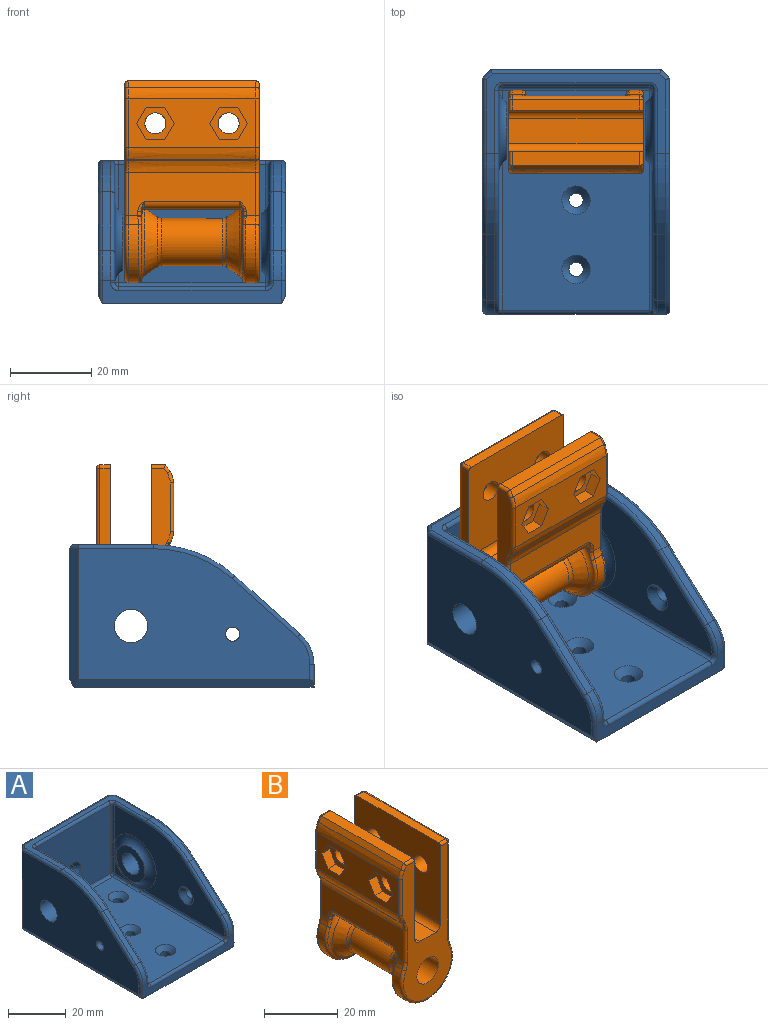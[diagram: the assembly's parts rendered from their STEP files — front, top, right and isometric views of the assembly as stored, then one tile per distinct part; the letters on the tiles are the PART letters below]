
ASSEMBLY  parts=2 mates=1
PART A: 87 faces, bbox 46x60.8x37.5 mm
  f0: plane 54x29mm, normal (1,0,0), area 820.2mm2, adj f28,f38,f46,f47,f48,f52,f57,f61
  f1: plane 54x29mm, normal (-1,0,0), area 820.2mm2, adj f31,f37,f59,f66,f67,f69,f71,f72
  f2: cylinder r=1.75mm len=3.5mm, axis (0,0,1), area 24.7mm2, adj f3,f6
  f3: cone r=1.75mm half-angle=45deg, axis (0,0,1), area 40.8mm2, adj f2,f11
  f4: plane 44x19.56mm, normal (0,0,1), area 157.9mm2, adj f39,f40,f62,f65,f68,f70,f72,f78
  f5: plane 57x32.27mm, normal (-1,0,0), area 1425.6mm2, adj f15,f27,f34,f36,f82,f83,f84,f85
  f6: plane 59x44mm, normal (0,0,-1), area 2557.5mm2, adj f2,f8,f17,f19,f21,f32,f33,f34
  f7: plane 57x32.27mm, normal (1,0,0), area 1425.6mm2, adj f14,f30,f32,f35,f74,f75,f76,f77
  f8: plane 44x5.52mm, normal (0,-1,0), area 143.8mm2, adj f6,f41,f42,f47,f53,f58,f63,f66
  f9: plane 42x32.27mm, normal (0,1,0), area 1345.6mm2, adj f23,f33,f35,f36,f80
  f10: plane 6.92x6.92mm, normal (1,0,0), area 15.9mm2, adj f38,f43,f51
  f11: plane 54x36mm, normal (0,0,1), area 1789.8mm2, adj f3,f18,f20,f22,f43,f44,f48,f49
  f12: plane 6.92x6.92mm, normal (-1,0,0), area 15.9mm2, adj f37,f49,f60
  f13: plane 36x29mm, normal (0,-1,0), area 1005.3mm2, adj f24,f50,f51,f56,f60,f61,f64,f67
  f14: cylinder r=4.1mm len=8.2mm, axis (-1,0,0), area 154.6mm2, adj f7,f29
  f15: cylinder r=4.1mm len=8.2mm, axis (-1,0,0), area 154.6mm2, adj f5,f16
  f16: plane 14x14mm, normal (1,0,0), area 101.1mm2, adj f15,f38
  f17: cylinder r=1.75mm len=3.5mm, axis (0,0,1), area 24.7mm2, adj f6,f18
  f18: cone r=1.75mm half-angle=45deg, axis (0,0,1), area 40.8mm2, adj f11,f17
  f19: cylinder r=1.75mm len=3.5mm, axis (0,0,1), area 24.7mm2, adj f6,f20
  f20: cone r=1.75mm half-angle=45deg, axis (0,0,1), area 40.8mm2, adj f11,f19
  f21: cylinder r=1.75mm len=3.5mm, axis (0,0,1), area 24.7mm2, adj f6,f22
  f22: cone r=1.75mm half-angle=45deg, axis (0,0,1), area 40.8mm2, adj f11,f21
  f23: cylinder r=1.75mm len=3.5mm, axis (0,-1,0), area 24.7mm2, adj f9,f24
  f24: cone r=1.75mm half-angle=45deg, axis (0,-1,0), area 40.8mm2, adj f13,f23
  f25: plane 16.12x14.4mm, normal (0,-0.67,0.75), area 43.2mm2, adj f39,f41,f52,f84
  f26: plane 16.12x14.4mm, normal (0,-0.67,0.75), area 43.2mm2, adj f40,f42,f71,f76
  f27: cylinder r=1.75mm len=3.5mm, axis (1,0,0), area 24.7mm2, adj f5,f28
  f28: cone r=1.75mm half-angle=45deg, axis (1,0,0), area 40.8mm2, adj f0,f27
  f29: plane 14x14mm, normal (-1,0,0), area 101.1mm2, adj f14,f37
  f30: cylinder r=1.75mm len=3.5mm, axis (-1,0,0), area 24.7mm2, adj f7,f31
  f31: cone r=1.75mm half-angle=45deg, axis (-1,0,0), area 40.8mm2, adj f1,f30
  f32: plane 59x1.73mm, normal (0.87,0,-0.5), area 116.6mm2, adj f6,f7,f35,f74
  f33: plane 44x1.73mm, normal (0,0.87,-0.5), area 86mm2, adj f6,f9,f35,f36
  f34: plane 59x1.73mm, normal (-0.87,0,-0.5), area 116.6mm2, adj f5,f6,f36,f86
  f35: plane 34x2mm, normal (0.71,0.71,0), area 93.7mm2, adj f7,f9,f32,f33,f79
  f36: plane 34x2mm, normal (-0.71,0.71,0), area 93.7mm2, adj f5,f9,f33,f34,f81
  f37: torus R=10.46mm, axis (1,0,0), area 220mm2, adj f1,f12,f29,f54,f64
  f38: torus R=10.46mm, axis (1,0,0), area 220mm2, adj f0,f10,f16,f44,f56
  f39: cylinder r=30mm len=19.98mm, axis (-1,0,0), area 43.7mm2, adj f4,f25,f57,f83
  f40: cylinder r=30mm len=19.98mm, axis (-1,0,0), area 43.7mm2, adj f4,f26,f73,f77
  f41: cylinder r=10mm len=7.46mm, axis (1,0,0), area 16.8mm2, adj f8,f25,f46,f85
  f42: cylinder r=10mm len=7.46mm, axis (1,0,0), area 16.8mm2, adj f8,f26,f69,f75
  f43: cylinder r=1mm len=6.92mm, axis (0,-1,0), area 10.9mm2, adj f10,f11,f44,f45
  f44: bspline ~7.51x1.17mm, area 10.3mm2, adj f11,f38,f43,f48
  f45: sphere r=1mm, area 1.6mm2, adj f43,f50,f51
  f46: torus R=9mm, axis (1,0,0), area 12.7mm2, adj f0,f41,f47,f52
  f47: cylinder r=1mm len=1mm, axis (0,0,-1), area 0.8mm2, adj f0,f8,f46,f53
  f48: cylinder r=1mm len=40.92mm, axis (0,-1,0), area 64.3mm2, adj f0,f11,f44,f53
  f49: cylinder r=1mm len=6.92mm, axis (0,1,0), area 10.9mm2, adj f11,f12,f54,f55
  f50: cylinder r=1mm len=36mm, axis (-1,0,0), area 56.5mm2, adj f11,f13,f45,f55
  f51: cylinder r=1mm len=6.92mm, axis (0,0,1), area 10.9mm2, adj f10,f13,f45,f56
  f52: cylinder r=1mm len=16.79mm, axis (0,0.75,0.67), area 34mm2, adj f0,f25,f46,f57
  f53: torus R=2mm, axis (0,-1,0), area 3.4mm2, adj f8,f47,f48,f58
  f54: bspline ~8.32x1.17mm, area 10.3mm2, adj f11,f37,f49,f59
  f55: sphere r=1mm, area 1.6mm2, adj f49,f50,f60
  f56: bspline ~8.32x1.17mm, area 10.3mm2, adj f13,f38,f51,f61
  f57: torus R=29mm, axis (1,0,0), area 33.9mm2, adj f0,f39,f52,f62
  f58: cylinder r=1mm len=36mm, axis (1,0,0), area 56.5mm2, adj f8,f11,f53,f63
  f59: cylinder r=1mm len=40.92mm, axis (0,1,0), area 64.3mm2, adj f1,f11,f54,f63
  f60: cylinder r=1mm len=6.92mm, axis (0,0,-1), area 10.9mm2, adj f12,f13,f55,f64
  f61: cylinder r=1mm len=15.92mm, axis (0,0,1), area 25mm2, adj f0,f13,f56,f65
  f62: cylinder r=1mm len=15.56mm, axis (0,1,0), area 24.4mm2, adj f0,f4,f57,f65
  f63: torus R=2mm, axis (0,-1,0), area 3.4mm2, adj f8,f58,f59,f66
  f64: bspline ~8.32x1.17mm, area 10.3mm2, adj f13,f37,f60,f67
  f65: torus R=2mm, axis (0,0,1), area 3.4mm2, adj f4,f61,f62,f68
  f66: cylinder r=1mm len=1mm, axis (0,0,1), area 0.8mm2, adj f1,f8,f63,f69
  f67: cylinder r=1mm len=15.92mm, axis (0,0,-1), area 25mm2, adj f1,f13,f64,f70
  f68: cylinder r=1mm len=36mm, axis (1,0,0), area 56.5mm2, adj f4,f13,f65,f70
  f69: torus R=9mm, axis (1,0,0), area 12.7mm2, adj f1,f42,f66,f71
  f70: torus R=2mm, axis (0,0,1), area 3.4mm2, adj f4,f67,f68,f72
  f71: cylinder r=1mm len=16.79mm, axis (0,0.75,0.67), area 34mm2, adj f1,f26,f69,f73
  f72: cylinder r=1mm len=15.56mm, axis (0,-1,0), area 24.4mm2, adj f1,f4,f70,f73
  f73: torus R=29mm, axis (1,0,0), area 33.9mm2, adj f1,f40,f71,f72
  f74: cylinder r=1mm len=5.52mm, axis (0,0,-1), area 6.9mm2, adj f7,f8,f32,f75
  f75: torus R=9mm, axis (1,0,0), area 12.7mm2, adj f7,f42,f74,f76
  f76: cylinder r=1mm len=16.79mm, axis (0,0.75,0.67), area 34mm2, adj f7,f26,f75,f77
  f77: torus R=29mm, axis (1,0,0), area 33.9mm2, adj f7,f40,f76,f78
  f78: cylinder r=1mm len=18.56mm, axis (0,1,0), area 28.9mm2, adj f4,f7,f77,f79
  f79: cylinder r=1mm len=2.71mm, axis (-0.71,0.71,0), area 4mm2, adj f4,f35,f78,f80
  f80: cylinder r=1mm len=42mm, axis (-1,0,0), area 65.5mm2, adj f4,f9,f79,f81
  f81: cylinder r=1mm len=2.71mm, axis (0.71,0.71,0), area 4mm2, adj f4,f36,f80,f82
  f82: cylinder r=1mm len=18.56mm, axis (0,-1,0), area 28.9mm2, adj f4,f5,f81,f83
  f83: torus R=29mm, axis (1,0,0), area 33.9mm2, adj f5,f39,f82,f84
  f84: cylinder r=1mm len=16.79mm, axis (0,0.75,0.67), area 34mm2, adj f5,f25,f83,f85
  f85: torus R=9mm, axis (1,0,0), area 12.7mm2, adj f5,f41,f84,f86
  f86: cylinder r=1mm len=5.52mm, axis (0,0,1), area 6.9mm2, adj f5,f8,f34,f85
PART B: 113 faces, bbox 24.6x36.3x51.9 mm
  f0: plane 1.29x0.97mm, normal (0,1,0), area 0.6mm2, adj f44,f109,f110,f111
  f1: plane 1.29x0.97mm, normal (0,-1,0), area 0.6mm2, adj f45,f95,f96,f98
  f2: cylinder r=10mm len=20mm, axis (0,1,0), area 101.1mm2, adj f50,f52,f75,f92
  f3: plane 31.4x11.99mm, normal (-1,0,0), area 265.7mm2, adj f20,f21,f22,f23,f24,f25,f28,f29
  f4: cylinder r=2.6mm len=5.2mm, axis (-1,0,0), area 40.8mm2, adj f6,f34
  f5: cylinder r=2.6mm len=5.2mm, axis (-1,0,0), area 40.8mm2, adj f6,f26
  f6: plane 33x26.5mm, normal (1,0,0), area 831.8mm2, adj f4,f5,f7,f17,f18,f48,f56,f82
  f7: plane 31.4x3.5mm, normal (0,0,1), area 109.9mm2, adj f6,f8,f56,f82
  f8: plane 31.4x1.57mm, normal (-0.82,0,0.57), area 60mm2, adj f7,f54,f57,f84
  f9: plane 31.4x0.27mm, normal (-0.82,0,-0.57), area 10.5mm2, adj f53,f55,f61,f79
  f10: plane 31.4x10.63mm, normal (-1,0,0), area 242.1mm2, adj f41,f49,f50,f55,f63,f77,f97,f98
  f11: cylinder r=10mm len=20mm, axis (0,1,0), area 101.1mm2, adj f49,f51,f65,f105
  f12: plane 32.26x31.4mm, normal (1,0,0), area 878.9mm2, adj f19,f27,f42,f51,f52,f67,f70,f73
  f13: plane 31.4x2.7mm, normal (0,0,1), area 84.8mm2, adj f14,f68,f70,f71
  f14: plane 33x26.5mm, normal (-1,0,0), area 831.8mm2, adj f13,f17,f18,f19,f27,f47,f68,f71
  f15: plane 33x6mm, normal (0,0,1), area 198mm2, adj f17,f18,f47,f48
  f16: cylinder r=4.1mm len=33mm, axis (0,1,0), area 850.1mm2, adj f17,f18
  f17: plane 48x18.9mm, normal (0,-1,0), area 447.9mm2, adj f6,f14,f15,f16,f47,f48,f56,f57
  f18: plane 48x18.9mm, normal (0,1,0), area 447.9mm2, adj f6,f14,f15,f16,f47,f48,f71,f73
  f19: cylinder r=2.6mm len=5.2mm, axis (-1,0,0), area 57.2mm2, adj f12,f14
  f20: plane 4.62x3mm, normal (0,0,-1), area 13.9mm2, adj f3,f21,f25,f26
  f21: plane 4x3mm, normal (0,-0.87,-0.5), area 13.9mm2, adj f3,f20,f22,f26
  f22: plane 4x3mm, normal (0,-0.87,0.5), area 13.9mm2, adj f3,f21,f23,f26
  f23: plane 4.62x3mm, normal (0,0,1), area 13.9mm2, adj f3,f22,f24,f26
  f24: plane 4x3mm, normal (0,0.87,0.5), area 13.9mm2, adj f3,f23,f25,f26
  f25: plane 4x3mm, normal (0,0.87,-0.5), area 13.9mm2, adj f3,f20,f24,f26
  f26: plane 9.24x8mm, normal (-1,0,0), area 34.2mm2, adj f5,f20,f21,f22,f23,f24,f25
  f27: cylinder r=2.6mm len=5.2mm, axis (-1,0,0), area 57.2mm2, adj f12,f14
  f28: plane 4.62x3mm, normal (0,0,-1), area 13.9mm2, adj f3,f29,f33,f34
  f29: plane 4x3mm, normal (0,-0.87,-0.5), area 13.9mm2, adj f3,f28,f30,f34
  f30: plane 4x3mm, normal (0,-0.87,0.5), area 13.9mm2, adj f3,f29,f31,f34
  f31: plane 4.62x3mm, normal (0,0,1), area 13.9mm2, adj f3,f30,f32,f34
  f32: plane 4x3mm, normal (0,0.87,0.5), area 13.9mm2, adj f3,f31,f33,f34
  f33: plane 4x3mm, normal (0,0.87,-0.5), area 13.9mm2, adj f3,f28,f32,f34
  f34: plane 9.24x8mm, normal (-1,0,0), area 34.2mm2, adj f4,f28,f29,f30,f31,f32,f33
  f35: cylinder r=10mm len=22.89mm, axis (0,-1,0), area 262mm2, adj f41,f42,f91,f106
  f36: cylinder r=5.8mm len=14.88mm, axis (0,-1,0), area 542.4mm2, adj f43,f46
  f37: cone r=5.8mm half-angle=35deg, axis (0,-1,0), area 169.6mm2, adj f43,f44
  f38: plane 1.29x0.97mm, normal (0,1,0), area 0.6mm2, adj f44,f99,f101,f102
  f39: plane 1.29x0.97mm, normal (0,-1,0), area 0.6mm2, adj f45,f86,f87,f88
  f40: cone r=5.8mm half-angle=35deg, axis (0,1,0), area 169.6mm2, adj f45,f46
  f41: cylinder r=2mm len=23.4mm, axis (0,-1,0), area 100mm2, adj f10,f35,f93,f95,f108,f110
  f42: cylinder r=2mm len=23.4mm, axis (0,-1,0), area 100mm2, adj f12,f35,f87,f89,f102,f104
  f43: torus R=7.8mm, axis (0,-1,0), area 45.5mm2, adj f36,f37
  f44: torus R=9.94mm, axis (0,-1,0), area 70.7mm2, adj f0,f37,f38,f103,f104,f105,f106,f107
  f45: torus R=9.94mm, axis (0,1,0), area 70.7mm2, adj f1,f39,f40,f89,f90,f91,f92,f93
  f46: torus R=7.8mm, axis (0,-1,0), area 45.5mm2, adj f36,f40
  f47: cylinder r=2mm len=33mm, axis (0,1,0), area 103.7mm2, adj f14,f15,f17,f18
  f48: cylinder r=2mm len=33mm, axis (0,-1,0), area 103.7mm2, adj f6,f15,f17,f18
  f49: bspline ~4.4x2.18mm, area 5.5mm2, adj f10,f11,f64,f107,f109
  f50: bspline ~4.4x2.18mm, area 5.5mm2, adj f2,f10,f76,f94,f96
  f51: bspline ~4.4x2.18mm, area 5.5mm2, adj f11,f12,f66,f101,f103
  f52: bspline ~4.4x2.18mm, area 5.5mm2, adj f2,f12,f74,f88,f90
  f53: bspline ~36.3x2.87mm, area 95.1mm2, adj f3,f9,f60,f80
  f54: bspline ~36.3x2.87mm, area 95.1mm2, adj f3,f8,f58,f83
  f55: bspline ~36.3x2.87mm, area 95.1mm2, adj f9,f10,f62,f78
  f56: cylinder r=0.8mm len=3.5mm, axis (1,0,0), area 4.1mm2, adj f6,f7,f17,f57
  f57: cylinder r=0.8mm len=2.02mm, axis (0.57,0,0.82), area 2.1mm2, adj f8,f17,f56,f58
  f58: bspline ~3.38x1.72mm, area 3.6mm2, adj f17,f54,f57,f59
  f59: cylinder r=0.8mm len=11.99mm, axis (0,0,1), area 15.1mm2, adj f3,f17,f58,f60
  f60: bspline ~3.38x1.72mm, area 3.6mm2, adj f17,f53,f59,f61
  f61: cylinder r=0.8mm len=0.85mm, axis (-0.57,0,0.82), area 0.4mm2, adj f9,f17,f60,f62
  f62: bspline ~3.69x1.74mm, area 4mm2, adj f17,f55,f61,f63
  f63: cylinder r=0.8mm len=10.63mm, axis (0,0,1), area 13.4mm2, adj f10,f17,f62,f64
  f64: bspline ~3.09x1.43mm, area 3mm2, adj f17,f49,f63,f65
  f65: torus R=9.2mm, axis (0,-1,0), area 49.3mm2, adj f11,f17,f64,f66
  f66: bspline ~3.09x1.43mm, area 3mm2, adj f17,f51,f65,f67
  f67: cylinder r=0.8mm len=32.26mm, axis (0,0,-1), area 40.5mm2, adj f12,f17,f66,f69
  f68: cylinder r=0.8mm len=2.7mm, axis (1,0,0), area 3.4mm2, adj f13,f14,f17,f69
  f69: sphere r=0.8mm, area 1mm2, adj f67,f68,f70
  f70: cylinder r=0.8mm len=31.4mm, axis (0,1,0), area 39.5mm2, adj f12,f13,f69,f72
  f71: cylinder r=0.8mm len=2.7mm, axis (-1,0,0), area 3.4mm2, adj f13,f14,f18,f72
  f72: sphere r=0.8mm, area 0.6mm2, adj f70,f71,f73
  f73: cylinder r=0.8mm len=32.26mm, axis (0,0,1), area 40.5mm2, adj f12,f18,f72,f74
  f74: bspline ~3.09x1.43mm, area 3mm2, adj f18,f52,f73,f75
  f75: torus R=9.2mm, axis (0,-1,0), area 49.3mm2, adj f2,f18,f74,f76
  f76: bspline ~3.09x1.43mm, area 3mm2, adj f18,f50,f75,f77
  f77: cylinder r=0.8mm len=10.63mm, axis (0,0,-1), area 13.4mm2, adj f10,f18,f76,f78
  f78: bspline ~3.69x1.74mm, area 4mm2, adj f18,f55,f77,f79
  f79: cylinder r=0.8mm len=0.85mm, axis (0.57,0,-0.82), area 0.4mm2, adj f9,f18,f78,f80
  f80: bspline ~3.38x1.72mm, area 3.6mm2, adj f18,f53,f79,f81
  f81: cylinder r=0.8mm len=11.99mm, axis (0,0,-1), area 15.1mm2, adj f3,f18,f80,f83
  f82: cylinder r=0.8mm len=3.5mm, axis (-1,0,0), area 4.1mm2, adj f6,f7,f18,f84
  f83: bspline ~3.38x1.72mm, area 3.6mm2, adj f18,f54,f81,f84
  f84: cylinder r=0.8mm len=2.02mm, axis (-0.57,0,-0.82), area 2.1mm2, adj f8,f18,f82,f83
  f85: bspline ~3x1.6mm, area 1.3mm2, adj f12,f86,f87
  f86: cylinder r=0.8mm len=1.02mm, axis (0,0,1), area 1.3mm2, adj f12,f39,f85,f88
  f87: torus R=2.8mm, axis (0,1,0), area 2.5mm2, adj f39,f42,f85,f89
  f88: bspline ~0.9x0.85mm, area 0.3mm2, adj f39,f52,f86,f90
  f89: bspline ~2.2x1.65mm, area 2.5mm2, adj f42,f45,f87,f91
  f90: bspline ~2.65x1.45mm, area 2.4mm2, adj f45,f52,f88,f92
  f91: torus R=9.2mm, axis (0,-1,0), area 19.4mm2, adj f35,f45,f89,f93
  f92: torus R=9.2mm, axis (0,1,0), area 41.3mm2, adj f2,f45,f90,f94
  f93: bspline ~2.2x1.65mm, area 2.5mm2, adj f41,f45,f91,f95
  f94: bspline ~2.65x1.45mm, area 2.4mm2, adj f45,f50,f92,f96
  f95: torus R=2.8mm, axis (0,1,0), area 2.5mm2, adj f1,f41,f93,f97
  f96: bspline ~0.83x0.8mm, area 0.3mm2, adj f1,f50,f94,f98
  f97: bspline ~3x1.6mm, area 1.3mm2, adj f10,f95,f98
  f98: cylinder r=0.8mm len=1.02mm, axis (0,0,1), area 1.3mm2, adj f1,f10,f96,f97
  f99: cylinder r=0.8mm len=1.02mm, axis (0,0,-1), area 1.3mm2, adj f12,f38,f100,f101
  f100: bspline ~3x1.6mm, area 1.3mm2, adj f12,f99,f102
  f101: bspline ~0.83x0.8mm, area 0.3mm2, adj f38,f51,f99,f103
  f102: torus R=2.8mm, axis (0,-1,0), area 2.5mm2, adj f38,f42,f100,f104
  f103: bspline ~2.44x1.35mm, area 2.4mm2, adj f44,f51,f101,f105
  f104: bspline ~2.2x1.65mm, area 2.5mm2, adj f42,f44,f102,f106
  f105: torus R=9.2mm, axis (0,1,0), area 41.3mm2, adj f11,f44,f103,f107
  f106: torus R=9.2mm, axis (0,1,0), area 19.4mm2, adj f35,f44,f104,f108
  f107: bspline ~2.65x1.45mm, area 2.4mm2, adj f44,f49,f105,f109
  f108: bspline ~2.2x1.65mm, area 2.5mm2, adj f41,f44,f106,f110
  f109: bspline ~0.9x0.85mm, area 0.3mm2, adj f0,f49,f107,f111
  f110: torus R=2.8mm, axis (0,-1,0), area 2.5mm2, adj f0,f41,f108,f112
  f111: cylinder r=0.8mm len=1.02mm, axis (0,0,-1), area 1.3mm2, adj f0,f10,f109,f112
  f112: bspline ~3x1.6mm, area 1.3mm2, adj f10,f110,f111
PLACE A t=(0.33,29.86,-17.99)mm fixed
PLACE B rot(axis=(0,0,1),90deg) t=(0.33,14.86,-2.99)mm
MATE revolute A.f37 <-> B.f16  axis (-1,0,0) through (17.33,14.86,-2.99)mm
